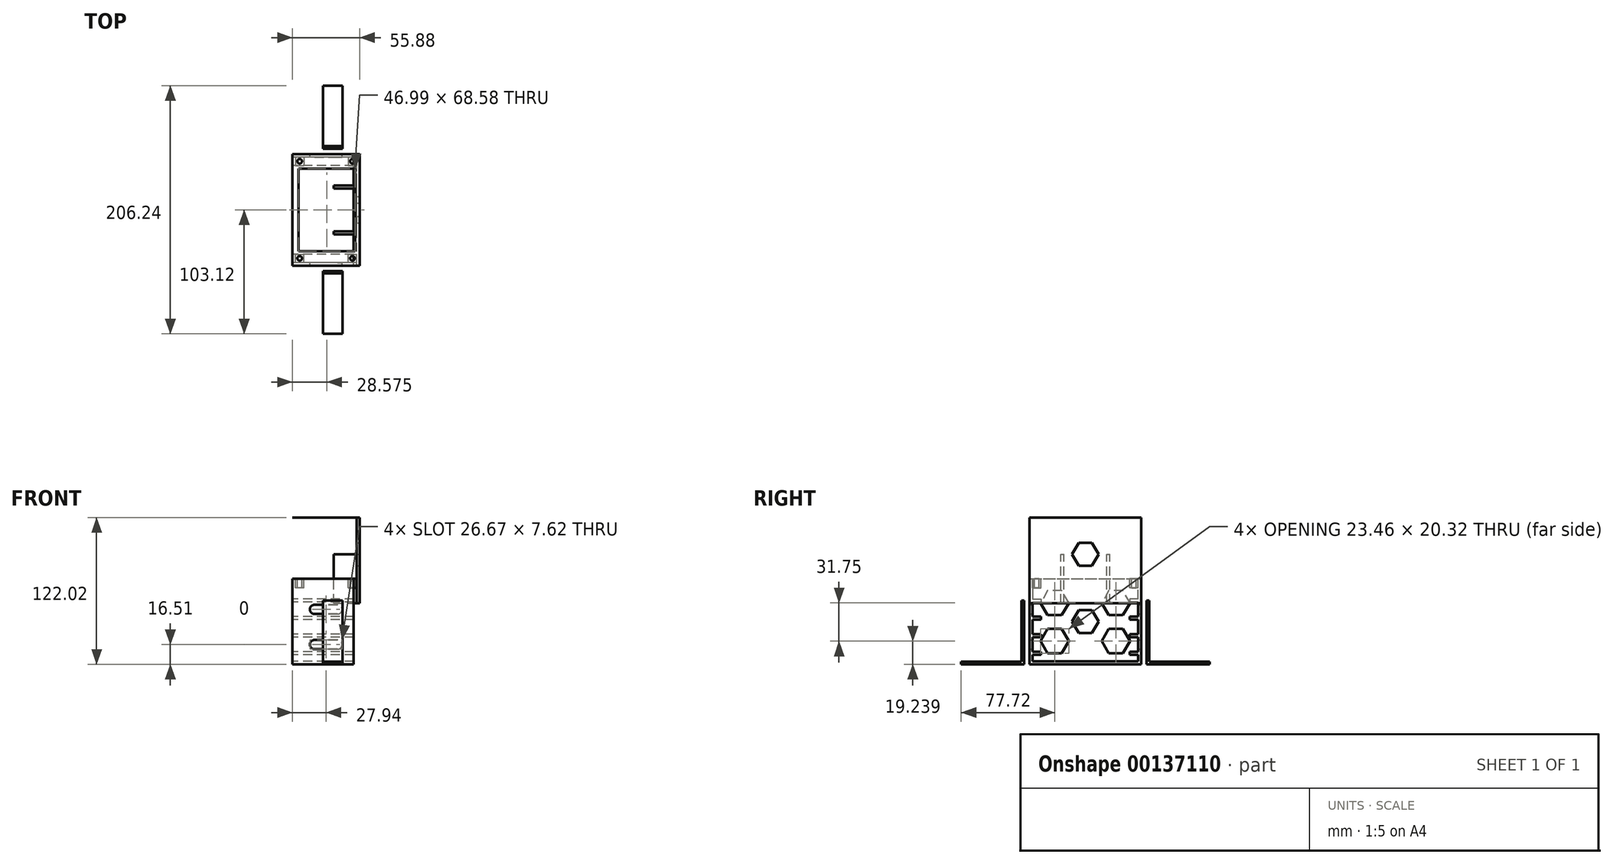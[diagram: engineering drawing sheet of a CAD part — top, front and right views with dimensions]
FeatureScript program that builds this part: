
annotation { "Feature Type Name" : "Feature", "Feature Type Description" : "" }
export const myFeature = defineFeature(function(context is Context, id is Id, definition is map)
    precondition{}
    {
        {
            assignVariable(context, id + "F0", {"name" : "sideWidth", "anyValue" : .1});
        }
        {
            var Q0;
            Q0=qCreatedBy(makeId("Right.planeOp"),FACE);
            var sketch = newSketch(context, id + "F1", { "sketchPlane" : qUnion([Q0])});
            skLineSegment(sketch, "E0.bottom", {"start": v(-50.8, 0) * mm, "end": v(-52.96, 0) * mm});
            skLineSegment(sketch, "E0.top", {"start": v(-50.8, 52.96) * mm, "end": v(-52.96, 52.96) * mm});
            skLineSegment(sketch, "E0.left", {"start": v(-50.8, 0) * mm, "end": v(-50.8, 52.96) * mm});
            skLineSegment(sketch, "E0.right", {"start": v(-52.96, 0) * mm, "end": v(-52.96, 52.96) * mm});
            skLineSegment(sketch, "E1.bottom", {"start": v(-50.8, 0) * mm, "end": v(-103.12, 0) * mm});
            skLineSegment(sketch, "E1.top", {"start": v(-50.8, 2.16) * mm, "end": v(-103.12, 2.16) * mm});
            skLineSegment(sketch, "E1.left", {"start": v(-50.8, 0) * mm, "end": v(-50.8, 2.16) * mm});
            skLineSegment(sketch, "E1.right", {"start": v(-103.12, 0) * mm, "end": v(-103.12, 2.16) * mm});
            skLineSegment(sketch, "E2.bottom", {"start": v(50.8, 0) * mm, "end": v(52.96, 0) * mm});
            skLineSegment(sketch, "E2.top", {"start": v(50.8, 52.96) * mm, "end": v(52.96, 52.96) * mm});
            skLineSegment(sketch, "E2.left", {"start": v(50.8, 0) * mm, "end": v(50.8, 52.96) * mm});
            skLineSegment(sketch, "E2.right", {"start": v(52.96, 0) * mm, "end": v(52.96, 52.96) * mm});
            skLineSegment(sketch, "E3.bottom", {"start": v(50.8, 0) * mm, "end": v(103.12, 0) * mm});
            skLineSegment(sketch, "E3.top", {"start": v(50.8, 2.16) * mm, "end": v(103.12, 2.16) * mm});
            skLineSegment(sketch, "E3.left", {"start": v(50.8, 0) * mm, "end": v(50.8, 2.16) * mm});
            skLineSegment(sketch, "E3.right", {"start": v(103.12, 0) * mm, "end": v(103.12, 2.16) * mm});
            skLineSegment(sketch, "E4", {"start": v(-50.8, 0) * mm, "end": v(0, 0) * mm, "construction": true});
            skLineSegment(sketch, "E5", {"start": v(0, 0) * mm, "end": v(50.8, 0) * mm, "construction": true});
            skSolve(sketch);
        }
        {
            var Q0;
            Q0 = qSketchRegion(id + "F1", true);
            extrude(context, id + "F2", {"entities" : qUnion([Q0]), "depth" : 16.13 * mm});
        }
        {
            var Q0;
            Q0=qCreatedBy(makeId("Right.planeOp"),FACE);
            cPlane(context, id + "F3", {"entities" : qUnion([Q0]), "cplaneType" : CPlaneType.OFFSET, "offset" : 25.4 * mm, "oppositeDirection" : true, "width" : 152.4 * mm, "height" : 152.4 * mm});
        }
        {
            var Q0;
            Q0=qCreatedBy(id+"F3.planeOp",FACE);
            var sketch = newSketch(context, id + "F4", { "sketchPlane" : qUnion([Q0])});
            skLineSegment(sketch, "E6.bottom", {"start": v(-46.35, 0) * mm, "end": v(46.35, 0) * mm});
            skLineSegment(sketch, "E6.top", {"start": v(-46.36, 71.12) * mm, "end": v(46.36, 71.12) * mm});
            skLineSegment(sketch, "E6.left", {"start": v(-46.35, 0) * mm, "end": v(-46.36, 71.12) * mm});
            skLineSegment(sketch, "E6.right", {"start": v(46.35, 0) * mm, "end": v(46.35, 71.12) * mm});
            skSolve(sketch);
        }
        {
            var Q0;
            Q0 = qSketchRegion(id + "F4", true);
            extrude(context, id + "F5", {"entities" : qUnion([Q0]), "depth" : (getVariable(context, 'sideWidth')) * mm});
        }
        {
            var Q0;
            Q0=makeQuery(id+"F5.opExtrude","CAP_FACE",FACE,{"disambiguationData":[OSD([sQuery(id+"F4.wireOp",EDGE,"E6.bottom"),sQuery(id+"F4.wireOp",EDGE,"E6.top"),sQuery(id+"F4.wireOp",EDGE,"E6.left"),sQuery(id+"F4.wireOp",EDGE,"E6.right")])],"isStart":false});
            var sketch = newSketch(context, id + "F6", { "sketchPlane" : qUnion([Q0])});
            skLineSegment(sketch, "E7.bottom", {"start": v(-46.36, 71.12) * mm, "end": v(-43.82, 71.12) * mm});
            skLineSegment(sketch, "E7.top", {"start": v(-46.36, 0) * mm, "end": v(-43.82, 0) * mm});
            skLineSegment(sketch, "E7.left", {"start": v(-46.36, 71.12) * mm, "end": v(-46.36, 0) * mm});
            skLineSegment(sketch, "E7.right", {"start": v(-43.82, 71.12) * mm, "end": v(-43.82, 0) * mm});
            skLineSegment(sketch, "E8.bottom", {"start": v(-46.36, 0) * mm, "end": v(46.36, 0) * mm});
            skLineSegment(sketch, "E8.top", {"start": v(-46.36, 2.54) * mm, "end": v(46.35, 2.54) * mm});
            skLineSegment(sketch, "E8.left", {"start": v(-46.36, 0) * mm, "end": v(-46.36, 2.54) * mm});
            skLineSegment(sketch, "E8.right", {"start": v(46.35, 0) * mm, "end": v(46.35, 2.54) * mm});
            skLineSegment(sketch, "E9.bottom", {"start": v(46.35, 0) * mm, "end": v(43.81, 0) * mm});
            skLineSegment(sketch, "E9.top", {"start": v(46.35, 71.12) * mm, "end": v(43.81, 71.12) * mm});
            skLineSegment(sketch, "E9.left", {"start": v(46.35, 0) * mm, "end": v(46.35, 71.12) * mm});
            skLineSegment(sketch, "E9.right", {"start": v(43.81, 0) * mm, "end": v(43.81, 71.12) * mm});
            skLineSegment(sketch, "E10.bottom", {"start": v(-46.36, 0) * mm, "end": v(-27.62, 0) * mm});
            skLineSegment(sketch, "E10.top", {"start": v(-46.36, 53.98) * mm, "end": v(-27.62, 53.98) * mm, "construction": true});
            skLineSegment(sketch, "E10.left", {"start": v(-46.36, 0) * mm, "end": v(-46.36, 53.98) * mm});
            skLineSegment(sketch, "E10.right", {"start": v(-27.62, 0) * mm, "end": v(-27.62, 53.98) * mm, "construction": true});
            skLineSegment(sketch, "E11.bottom", {"start": v(46.35, 0) * mm, "end": v(27.62, 0) * mm});
            skLineSegment(sketch, "E11.top", {"start": v(46.35, 53.98) * mm, "end": v(27.62, 53.98) * mm, "construction": true});
            skLineSegment(sketch, "E11.left", {"start": v(46.36, 0) * mm, "end": v(46.35, 53.98) * mm});
            skLineSegment(sketch, "E11.right", {"start": v(27.62, 0) * mm, "end": v(27.62, 53.98) * mm, "construction": true});
            skLineSegment(sketch, "E12", {"start": v(-27.62, 53.98) * mm, "end": v(27.62, 53.98) * mm, "construction": true});
            skLineSegment(sketch, "E13.bottom", {"start": v(-43.82, 54.42) * mm, "end": v(-36.83, 54.42) * mm});
            skLineSegment(sketch, "E13.top", {"start": v(-43.82, 51.88) * mm, "end": v(-36.83, 51.88) * mm});
            skLineSegment(sketch, "E13.left", {"start": v(-43.82, 54.42) * mm, "end": v(-43.82, 51.88) * mm});
            skLineSegment(sketch, "E13.right", {"start": v(-36.83, 54.42) * mm, "end": v(-36.83, 51.88) * mm});
            skLineSegment(sketch, "E14.bottom", {"start": v(-43.82, 39.56) * mm, "end": v(-36.83, 39.56) * mm});
            skLineSegment(sketch, "E14.top", {"start": v(-43.82, 37.02) * mm, "end": v(-36.83, 37.02) * mm});
            skLineSegment(sketch, "E14.left", {"start": v(-43.82, 39.56) * mm, "end": v(-43.82, 37.02) * mm});
            skLineSegment(sketch, "E14.right", {"start": v(-36.83, 39.56) * mm, "end": v(-36.83, 37.02) * mm});
            skLineSegment(sketch, "E15.bottom", {"start": v(-43.82, 25.2) * mm, "end": v(-36.83, 25.2) * mm});
            skLineSegment(sketch, "E15.top", {"start": v(-43.82, 22.67) * mm, "end": v(-36.83, 22.67) * mm});
            skLineSegment(sketch, "E15.left", {"start": v(-43.82, 25.2) * mm, "end": v(-43.82, 22.67) * mm});
            skLineSegment(sketch, "E15.right", {"start": v(-36.83, 25.2) * mm, "end": v(-36.83, 22.67) * mm});
            skLineSegment(sketch, "E16.bottom", {"start": v(-43.82, 10.35) * mm, "end": v(-36.83, 10.35) * mm});
            skLineSegment(sketch, "E16.top", {"start": v(-43.82, 7.81) * mm, "end": v(-36.83, 7.81) * mm});
            skLineSegment(sketch, "E16.left", {"start": v(-43.82, 10.35) * mm, "end": v(-43.82, 7.81) * mm});
            skLineSegment(sketch, "E16.right", {"start": v(-36.83, 10.35) * mm, "end": v(-36.83, 7.81) * mm});
            skLineSegment(sketch, "E17.bottom", {"start": v(43.81, 54.42) * mm, "end": v(36.83, 54.42) * mm});
            skLineSegment(sketch, "E17.top", {"start": v(43.81, 51.88) * mm, "end": v(36.83, 51.88) * mm});
            skLineSegment(sketch, "E17.left", {"start": v(43.81, 54.42) * mm, "end": v(43.81, 51.88) * mm});
            skLineSegment(sketch, "E17.right", {"start": v(36.83, 54.42) * mm, "end": v(36.83, 51.88) * mm});
            skLineSegment(sketch, "E18.bottom", {"start": v(43.81, 39.56) * mm, "end": v(36.83, 39.56) * mm});
            skLineSegment(sketch, "E18.top", {"start": v(43.81, 37.02) * mm, "end": v(36.83, 37.02) * mm});
            skLineSegment(sketch, "E18.left", {"start": v(43.81, 39.56) * mm, "end": v(43.81, 37.02) * mm});
            skLineSegment(sketch, "E18.right", {"start": v(36.83, 39.56) * mm, "end": v(36.83, 37.02) * mm});
            skLineSegment(sketch, "E19.bottom", {"start": v(43.81, 25.2) * mm, "end": v(36.83, 25.2) * mm});
            skLineSegment(sketch, "E19.top", {"start": v(43.81, 22.67) * mm, "end": v(36.83, 22.67) * mm});
            skLineSegment(sketch, "E19.left", {"start": v(43.81, 25.2) * mm, "end": v(43.81, 22.67) * mm});
            skLineSegment(sketch, "E19.right", {"start": v(36.83, 25.2) * mm, "end": v(36.83, 22.67) * mm});
            skLineSegment(sketch, "E20.bottom", {"start": v(43.81, 10.35) * mm, "end": v(36.83, 10.35) * mm});
            skLineSegment(sketch, "E20.top", {"start": v(43.81, 7.81) * mm, "end": v(36.83, 7.81) * mm});
            skLineSegment(sketch, "E20.left", {"start": v(43.81, 10.35) * mm, "end": v(43.81, 7.81) * mm});
            skLineSegment(sketch, "E20.right", {"start": v(36.83, 10.35) * mm, "end": v(36.83, 7.81) * mm});
            skLineSegment(sketch, "E21", {"start": v(-36.83, 51.88) * mm, "end": v(-36.83, 39.56) * mm, "construction": true});
            skLineSegment(sketch, "E22", {"start": v(-36.83, 22.67) * mm, "end": v(-36.83, 10.35) * mm, "construction": true});
            skLineSegment(sketch, "E23", {"start": v(36.83, 51.88) * mm, "end": v(36.83, 39.56) * mm, "construction": true});
            skLineSegment(sketch, "E24", {"start": v(36.83, 22.67) * mm, "end": v(36.83, 10.35) * mm, "construction": true});
            skPoint(sketch, "E25", {"position": v(-36.83, 45.72) * mm});
            skPoint(sketch, "E26", {"position": v(-36.83, 16.51) * mm});
            skSolve(sketch);
        }
        {
            var Q0;
            Q0 = qSketchRegion(id + "F6", true);
            extrude(context, id + "F7", {"entities" : qUnion([Q0]), "operationType" : NewBodyOperationType.ADD, "depth" : 50.8 * mm});
        }
        {
            var Q0;
            Q0=makeQuery(id+"F7.boolean.opBoolean","MERGE",FACE,{"derivedFrom":[makeQuery(id+"F5.opExtrude","SWEPT_FACE",FACE,{"disambiguationData":[OSD([sQuery(id+"F4.wireOp",EDGE,"E6.top")])]}),makeQuery(id+"F7.opExtrude","SWEPT_FACE",FACE,{"disambiguationData":[OSD([sQuery(id+"F6.wireOp",EDGE,"E7.bottom")])]}),makeQuery(id+"F7.opExtrude","SWEPT_FACE",FACE,{"disambiguationData":[OSD([sQuery(id+"F6.wireOp",EDGE,"E9.top")])]})]});
            var sketch = newSketch(context, id + "F8", { "sketchPlane" : qUnion([Q0])});
            skLineSegment(sketch, "E27.bottom", {"start": v(-22.86, 43.81) * mm, "end": v(-15.88, 43.81) * mm});
            skLineSegment(sketch, "E27.top", {"start": v(-22.86, 36.83) * mm, "end": v(-15.88, 36.83) * mm});
            skLineSegment(sketch, "E27.left", {"start": v(-22.86, 43.81) * mm, "end": v(-22.86, 36.83) * mm});
            skLineSegment(sketch, "E27.right", {"start": v(-15.88, 43.81) * mm, "end": v(-15.88, 36.83) * mm});
            skLineSegment(sketch, "E28.bottom", {"start": v(20.96, 43.81) * mm, "end": v(27.94, 43.81) * mm});
            skLineSegment(sketch, "E28.top", {"start": v(20.96, 36.83) * mm, "end": v(27.94, 36.83) * mm});
            skLineSegment(sketch, "E28.left", {"start": v(20.96, 43.81) * mm, "end": v(20.96, 36.83) * mm});
            skLineSegment(sketch, "E28.right", {"start": v(27.94, 43.81) * mm, "end": v(27.94, 36.83) * mm});
            skLineSegment(sketch, "E29.bottom", {"start": v(-22.86, -43.82) * mm, "end": v(-15.87, -43.82) * mm});
            skLineSegment(sketch, "E29.top", {"start": v(-22.86, -36.83) * mm, "end": v(-15.87, -36.83) * mm});
            skLineSegment(sketch, "E29.left", {"start": v(-22.86, -43.81) * mm, "end": v(-22.86, -36.83) * mm});
            skLineSegment(sketch, "E29.right", {"start": v(-15.87, -43.81) * mm, "end": v(-15.87, -36.83) * mm});
            skLineSegment(sketch, "E30.bottom", {"start": v(20.96, -43.82) * mm, "end": v(27.94, -43.82) * mm});
            skLineSegment(sketch, "E30.top", {"start": v(20.96, -36.83) * mm, "end": v(27.94, -36.83) * mm});
            skLineSegment(sketch, "E30.left", {"start": v(20.96, -43.81) * mm, "end": v(20.96, -36.83) * mm});
            skLineSegment(sketch, "E30.right", {"start": v(27.94, -43.81) * mm, "end": v(27.94, -36.83) * mm});
            skCircle(sketch, "E31", {"center": v(-19.37, 40.32) * mm, "radius": 1.9 * mm});
            skPoint(sketch, "E31.centerSnap0", {"position": v(-19.37, 36.83) * mm});
            skPoint(sketch, "E31.centerSnap1", {"position": v(-15.88, 40.32) * mm});
            skCircle(sketch, "E32", {"center": v(24.45, 40.32) * mm, "radius": 1.9 * mm});
            skPoint(sketch, "E32.centerSnap0", {"position": v(24.45, 36.83) * mm});
            skPoint(sketch, "E32.centerSnap1", {"position": v(27.94, 40.32) * mm});
            skCircle(sketch, "E33", {"center": v(24.45, -40.32) * mm, "radius": 1.9 * mm});
            skPoint(sketch, "E33.centerSnap0", {"position": v(24.45, -43.82) * mm});
            skPoint(sketch, "E33.centerSnap1", {"position": v(27.94, -40.32) * mm});
            skCircle(sketch, "E34", {"center": v(-19.37, -40.32) * mm, "radius": 1.9 * mm});
            skPoint(sketch, "E34.centerSnap0", {"position": v(-19.37, -43.82) * mm});
            skPoint(sketch, "E34.centerSnap1", {"position": v(-15.87, -40.32) * mm});
            skSolve(sketch);
        }
        {
            var Q0;
            Q0 = qSketchRegion(id + "F8", true);
            extrude(context, id + "F9", {"entities" : qUnion([Q0]), "operationType" : NewBodyOperationType.ADD, "oppositeDirection" : true, "depth" : 7.62 * mm});
        }
        {
            var Q0;
            {var subQ0=sQuery(id+"F6.wireOp",EDGE,"E7.right");Q0=makeQuery(id+"F7.opExtrude","SWEPT_FACE",FACE,{"disambiguationData":[OSD([subQ0]),TDD([makeQuery(id+"F6.imprint","IMPRINT",EDGE,{"disambiguationData":[TD([[makeQuery(id+"F6.imprint","INTERSECT",VERTEX,{"derivedFrom":[subQ0,sQuery(id+"F6.wireOp",EDGE,"E13.top"),sQuery(id+"F6.wireOp",EDGE,"E13.left")]}),-1.0]])],"derivedFrom":subQ0})])]});}
            var sketch = newSketch(context, id + "F10", { "sketchPlane" : qUnion([Q0])});
            skLineSegment(sketch, "E35.bottom", {"start": v(-12.07, 49.53) * mm, "end": v(6.98, 49.53) * mm});
            skLineSegment(sketch, "E35.top", {"start": v(-12.07, 41.91) * mm, "end": v(6.98, 41.91) * mm});
            skLineSegment(sketch, "E35.left", {"start": v(-12.07, 49.53) * mm, "end": v(-12.07, 41.91) * mm});
            skLineSegment(sketch, "E35.right", {"start": v(6.98, 49.53) * mm, "end": v(6.98, 41.91) * mm});
            skLineSegment(sketch, "E36.bottom", {"start": v(-12.07, 20.32) * mm, "end": v(6.98, 20.32) * mm});
            skLineSegment(sketch, "E36.top", {"start": v(-12.07, 12.7) * mm, "end": v(6.98, 12.7) * mm});
            skLineSegment(sketch, "E36.left", {"start": v(-12.07, 20.32) * mm, "end": v(-12.07, 12.7) * mm});
            skLineSegment(sketch, "E36.right", {"start": v(6.98, 20.32) * mm, "end": v(6.98, 12.7) * mm});
            skArc(sketch, "E37", {"start": v(-12.07, 49.53) * mm, "mid": v(-15.88, 45.72) * mm, "end": v(-12.07, 41.91) * mm});
            skArc(sketch, "E38", {"start": v(6.98, 41.91) * mm, "mid": v(10.8, 45.72) * mm, "end": v(6.98, 49.53) * mm});
            skArc(sketch, "E39", {"start": v(-12.07, 20.32) * mm, "mid": v(-15.88, 16.51) * mm, "end": v(-12.07, 12.7) * mm});
            skArc(sketch, "E40", {"start": v(6.98, 12.7) * mm, "mid": v(10.8, 16.51) * mm, "end": v(6.98, 20.32) * mm});
            skPoint(sketch, "E41", {"position": v(-2.54, 41.91) * mm});
            skPoint(sketch, "E42", {"position": v(-2.54, 20.32) * mm});
            skLineSegment(sketch, "E43", {"start": v(-27.94, 39.56) * mm, "end": v(-27.94, 51.88) * mm, "construction": true});
            skLineSegment(sketch, "E44", {"start": v(-27.94, 22.67) * mm, "end": v(-27.94, 10.35) * mm, "construction": true});
            skPoint(sketch, "E45", {"position": v(-27.94, 16.51) * mm});
            skPoint(sketch, "E46", {"position": v(-27.94, 45.72) * mm});
            skSolve(sketch);
        }
        {
            var Q0;
            Q0 = qSketchRegion(id + "F10", true);
            extrude(context, id + "F11", {"entities" : qUnion([Q0]), "operationType" : NewBodyOperationType.REMOVE, "endBound" : BoundingType.UP_TO_NEXT, "oppositeDirection" : true, "depth" : 25.4 * mm, "hasSecondDirection" : true, "secondDirectionBound" : SecondDirectionBoundingType.THROUGH_ALL, "secondDirectionOppositeDirection" : false, "secondDirectionDepth" : 25.4 * mm});
        }
        {
            var Q0;
            Q0=makeQuery(id+"F7.opExtrude","SWEPT_FACE",FACE,{"disambiguationData":[OSD([sQuery(id+"F6.wireOp",EDGE,"E8.top")])]});
            var sketch = newSketch(context, id + "F12", { "sketchPlane" : qUnion([Q0])});
            skLineSegment(sketch, "E47", {"start": v(5.72, -43.82) * mm, "end": v(5.71, 43.81) * mm, "construction": true});
            skCircle(sketch, "E48", {"center": v(5.71, 20.32) * mm, "radius": 1.59 * mm});
            skCircle(sketch, "E49", {"center": v(5.72, -20.32) * mm, "radius": 1.59 * mm});
            skPoint(sketch, "E50", {"position": v(5.72, 0) * mm});
            skSolve(sketch);
        }
        {
            var Q0;
            Q0=makeQuery(id+"F9.boolean.opBoolean","MERGE",FACE,{"derivedFrom":[makeQuery(id+"F7.boolean.opBoolean","MERGE",FACE,{"derivedFrom":[makeQuery(id+"F5.opExtrude","SWEPT_FACE",FACE,{"disambiguationData":[OSD([sQuery(id+"F4.wireOp",EDGE,"E6.top")])]}),makeQuery(id+"F7.opExtrude","SWEPT_FACE",FACE,{"disambiguationData":[OSD([sQuery(id+"F6.wireOp",EDGE,"E7.bottom")])]}),makeQuery(id+"F7.opExtrude","SWEPT_FACE",FACE,{"disambiguationData":[OSD([sQuery(id+"F6.wireOp",EDGE,"E9.top")])]})]}),makeQuery(id+"F9.opExtrude","CAP_FACE",FACE,{"disambiguationData":[OSD([sQuery(id+"F8.wireOp",EDGE,"E27.bottom"),sQuery(id+"F8.wireOp",EDGE,"E27.top"),sQuery(id+"F8.wireOp",EDGE,"E27.left"),sQuery(id+"F8.wireOp",EDGE,"E27.right"),sQuery(id+"F8.wireOp",EDGE,"E31")])],"isStart":true}),makeQuery(id+"F9.opExtrude","CAP_FACE",FACE,{"disambiguationData":[OSD([sQuery(id+"F8.wireOp",EDGE,"E28.bottom"),sQuery(id+"F8.wireOp",EDGE,"E28.top"),sQuery(id+"F8.wireOp",EDGE,"E28.left"),sQuery(id+"F8.wireOp",EDGE,"E28.right"),sQuery(id+"F8.wireOp",EDGE,"E32")])],"isStart":true}),makeQuery(id+"F9.opExtrude","CAP_FACE",FACE,{"disambiguationData":[OSD([sQuery(id+"F8.wireOp",EDGE,"E29.bottom"),sQuery(id+"F8.wireOp",EDGE,"E29.top"),sQuery(id+"F8.wireOp",EDGE,"E29.left"),sQuery(id+"F8.wireOp",EDGE,"E29.right"),sQuery(id+"F8.wireOp",EDGE,"E34")])],"isStart":true}),makeQuery(id+"F9.opExtrude","CAP_FACE",FACE,{"disambiguationData":[OSD([sQuery(id+"F8.wireOp",EDGE,"E30.bottom"),sQuery(id+"F8.wireOp",EDGE,"E30.top"),sQuery(id+"F8.wireOp",EDGE,"E30.left"),sQuery(id+"F8.wireOp",EDGE,"E30.right"),sQuery(id+"F8.wireOp",EDGE,"E33")])],"isStart":true})]});
            cPlane(context, id + "F13", {"entities" : qUnion([Q0]), "cplaneType" : CPlaneType.OFFSET, "offset" : 50.8 * mm, "width" : 152.4 * mm, "height" : 152.4 * mm});
        }
        {
            var Q0;
            Q0=qCreatedBy(id+"F13.planeOp",FACE);
            var sketch = newSketch(context, id + "F14", { "sketchPlane" : qUnion([Q0])});
            skLineSegment(sketch, "E51.bottom", {"start": v(27.94, -46.36) * mm, "end": v(-25.4, -46.36) * mm});
            skLineSegment(sketch, "E51.top", {"start": v(27.94, 46.35) * mm, "end": v(-25.4, 46.35) * mm});
            skLineSegment(sketch, "E51.left", {"start": v(27.94, -46.36) * mm, "end": v(27.94, 46.35) * mm});
            skLineSegment(sketch, "E51.right", {"start": v(-25.4, -46.36) * mm, "end": v(-25.4, 46.35) * mm});
            skLineSegment(sketch, "E52.bottom", {"start": v(-20.32, 34.29) * mm, "end": v(26.67, 34.3) * mm});
            skLineSegment(sketch, "E52.top", {"start": v(-20.32, -34.3) * mm, "end": v(26.67, -34.3) * mm});
            skLineSegment(sketch, "E52.left", {"start": v(-20.32, 34.29) * mm, "end": v(-20.32, -34.3) * mm});
            skLineSegment(sketch, "E52.right", {"start": v(26.67, 34.3) * mm, "end": v(26.67, -34.3) * mm});
            skLineSegment(sketch, "E53", {"start": v(3.17, 36.83) * mm, "end": v(3.17, 34.29) * mm, "construction": true});
            skLineSegment(sketch, "E54", {"start": v(-20.32, 0) * mm, "end": v(-22.86, 0) * mm, "construction": true});
            skLineSegment(sketch, "E55", {"start": v(26.67, 0) * mm, "end": v(29.2, 0) * mm, "construction": true});
            skLineSegment(sketch, "E56", {"start": v(3.18, -34.3) * mm, "end": v(3.18, -36.83) * mm, "construction": true});
            skLineSegment(sketch, "E57.bottom", {"start": v(27.94, -46.36) * mm, "end": v(30.48, -46.36) * mm});
            skLineSegment(sketch, "E57.top", {"start": v(27.94, 46.35) * mm, "end": v(30.48, 46.35) * mm});
            skLineSegment(sketch, "E57.right", {"start": v(30.48, -46.36) * mm, "end": v(30.48, 46.35) * mm});
            skCircle(sketch, "E58", {"center": v(-19.37, 40.32) * mm, "radius": 1.9 * mm});
            skCircle(sketch, "E59", {"center": v(24.45, 40.32) * mm, "radius": 1.9 * mm});
            skCircle(sketch, "E60", {"center": v(-19.37, -40.32) * mm, "radius": 1.9 * mm});
            skCircle(sketch, "E61", {"center": v(24.45, -40.32) * mm, "radius": 1.9 * mm});
            skSolve(sketch);
        }
        {
            var Q0;
            Q0 = qSketchRegion(id + "F14", true);
            extrude(context, id + "F15", {"entities" : qUnion([Q0]), "depth" : (getVariable(context, 'sideWidth')) * mm});
        }
        {
            var Q0;
            Q0=makeQuery(id+"F15.opExtrude","CAP_FACE",FACE,{"disambiguationData":[OSD([sQuery(id+"F14.wireOp",EDGE,"E51.bottom"),sQuery(id+"F14.wireOp",EDGE,"E51.top"),sQuery(id+"F14.wireOp",EDGE,"E51.right"),sQuery(id+"F14.wireOp",EDGE,"E52.bottom"),sQuery(id+"F14.wireOp",EDGE,"E52.top"),sQuery(id+"F14.wireOp",EDGE,"E52.left"),sQuery(id+"F14.wireOp",EDGE,"E52.right"),sQuery(id+"F14.wireOp",EDGE,"E57.bottom"),sQuery(id+"F14.wireOp",EDGE,"E57.top"),sQuery(id+"F14.wireOp",EDGE,"E57.right")])],"isStart":true});
            var sketch = newSketch(context, id + "F16", { "sketchPlane" : qUnion([Q0])});
            skLineSegment(sketch, "E62.bottom", {"start": v(30.48, 46.36) * mm, "end": v(27.94, 46.36) * mm});
            skLineSegment(sketch, "E62.top", {"start": v(30.48, -46.35) * mm, "end": v(27.94, -46.35) * mm});
            skLineSegment(sketch, "E62.left", {"start": v(30.48, 46.36) * mm, "end": v(30.48, -46.35) * mm});
            skLineSegment(sketch, "E62.right", {"start": v(27.94, 46.36) * mm, "end": v(27.94, -46.35) * mm});
            skSolve(sketch);
        }
        {
            var Q0;
            Q0 = qSketchRegion(id + "F16", true);
            extrude(context, id + "F17", {"entities" : qUnion([Q0]), "operationType" : NewBodyOperationType.ADD, "depth" : 71.12 * mm});
        }
        {
            var Q0;
            Q0=makeQuery(id+"F17.boolean.opBoolean","MERGE",FACE,{"derivedFrom":[makeQuery(id+"F15.opExtrude","SWEPT_FACE",FACE,{"disambiguationData":[OSD([sQuery(id+"F14.wireOp",EDGE,"E57.right")])]}),makeQuery(id+"F17.opExtrude","SWEPT_FACE",FACE,{"disambiguationData":[OSD([sQuery(id+"F16.wireOp",EDGE,"E62.left")])]})]});
            var sketch = newSketch(context, id + "F18", { "sketchPlane" : qUnion([Q0])});
            skCircle(sketch, "E63.cCircle", {"center": v(0, 91.44) * mm, "radius": 9.53 * mm, "construction": true});
            skPoint(sketch, "E63.cCircle.centerSnap0", {"position": v(0, 50.8) * mm});
            skLineSegment(sketch, "E63.0", {"start": v(-5.5, 100.97) * mm, "end": v(5.5, 100.97) * mm});
            skLineSegment(sketch, "E63.1", {"start": v(5.5, 100.97) * mm, "end": v(11, 91.44) * mm});
            skLineSegment(sketch, "E63.2", {"start": v(11, 91.44) * mm, "end": v(5.5, 81.92) * mm});
            skLineSegment(sketch, "E63.3", {"start": v(5.5, 81.92) * mm, "end": v(-5.5, 81.92) * mm});
            skLineSegment(sketch, "E63.4", {"start": v(-5.5, 81.92) * mm, "end": v(-11, 91.44) * mm});
            skLineSegment(sketch, "E63.5", {"start": v(-11, 91.44) * mm, "end": v(-5.5, 100.97) * mm});
            skPoint(sketch, "E63.0.midPoint", {"position": v(0, 100.97) * mm});
            skSolve(sketch);
        }
        {
            var Q0;
            Q0 = qSketchRegion(id + "F18", true);
            extrude(context, id + "F19", {"entities" : qUnion([Q0]), "operationType" : NewBodyOperationType.REMOVE, "endBound" : BoundingType.UP_TO_NEXT, "oppositeDirection" : true, "depth" : 25.4 * mm});
        }
        {
            var Q0;
            Q0=makeQuery(id+"F17.opExtrude","SWEPT_FACE",FACE,{"disambiguationData":[OSD([sQuery(id+"F16.wireOp",EDGE,"E62.right")])]});
            var sketch = newSketch(context, id + "F20", { "sketchPlane" : qUnion([Q0])});
            skLineSegment(sketch, "E64.bottom", {"start": v(20.32, 50.8) * mm, "end": v(17.78, 50.8) * mm});
            skLineSegment(sketch, "E64.top", {"start": v(20.32, 91.44) * mm, "end": v(17.78, 91.44) * mm});
            skLineSegment(sketch, "E64.left", {"start": v(20.32, 50.8) * mm, "end": v(20.32, 91.44) * mm});
            skLineSegment(sketch, "E64.right", {"start": v(17.78, 50.8) * mm, "end": v(17.78, 91.44) * mm});
            skLineSegment(sketch, "E65.bottom", {"start": v(-17.78, 50.8) * mm, "end": v(-20.32, 50.8) * mm});
            skLineSegment(sketch, "E65.top", {"start": v(-17.78, 91.44) * mm, "end": v(-20.32, 91.44) * mm});
            skLineSegment(sketch, "E65.left", {"start": v(-17.78, 50.8) * mm, "end": v(-17.78, 91.44) * mm});
            skLineSegment(sketch, "E65.right", {"start": v(-20.32, 50.8) * mm, "end": v(-20.32, 91.44) * mm});
            skLineSegment(sketch, "E66", {"start": v(17.78, 71.12) * mm, "end": v(-17.78, 71.12) * mm, "construction": true});
            skPoint(sketch, "E67", {"position": v(0, 71.12) * mm});
            skSolve(sketch);
        }
        {
            var Q0;
            Q0 = qSketchRegion(id + "F20", true);
            extrude(context, id + "F21", {"entities" : qUnion([Q0]), "operationType" : NewBodyOperationType.ADD, "depth" : 19.05 * mm});
        }
        {
            var Q0;
            Q0=makeQuery(id+"F5.opExtrude","CAP_FACE",FACE,{"disambiguationData":[OSD([sQuery(id+"F4.wireOp",EDGE,"E6.bottom"),sQuery(id+"F4.wireOp",EDGE,"E6.top"),sQuery(id+"F4.wireOp",EDGE,"E6.left"),sQuery(id+"F4.wireOp",EDGE,"E6.right")])],"isStart":true});
            var sketch = newSketch(context, id + "F22", { "sketchPlane" : qUnion([Q0])});
            skCircle(sketch, "E68.cCircle", {"center": v(0, 35.56) * mm, "radius": 9.53 * mm, "construction": true});
            skLineSegment(sketch, "E68.0", {"start": v(-5.5, 45.09) * mm, "end": v(5.5, 45.09) * mm});
            skLineSegment(sketch, "E68.1", {"start": v(5.5, 45.09) * mm, "end": v(11, 35.56) * mm});
            skLineSegment(sketch, "E68.2", {"start": v(11, 35.56) * mm, "end": v(5.5, 26.04) * mm});
            skLineSegment(sketch, "E68.3", {"start": v(5.5, 26.04) * mm, "end": v(-5.5, 26.04) * mm});
            skLineSegment(sketch, "E68.4", {"start": v(-5.5, 26.04) * mm, "end": v(-11, 35.56) * mm});
            skLineSegment(sketch, "E68.5", {"start": v(-11, 35.56) * mm, "end": v(-5.5, 45.08) * mm});
            skPoint(sketch, "E68.0.midPoint", {"position": v(0, 45.08) * mm});
            skCircle(sketch, "E69.cCircle", {"center": v(-25.4, 50.99) * mm, "radius": 10.16 * mm, "construction": true});
            skLineSegment(sketch, "E69.0", {"start": v(-31.27, 61.15) * mm, "end": v(-19.53, 61.15) * mm});
            skLineSegment(sketch, "E69.1", {"start": v(-19.53, 61.15) * mm, "end": v(-13.67, 50.99) * mm});
            skLineSegment(sketch, "E69.2", {"start": v(-13.67, 50.99) * mm, "end": v(-19.53, 40.83) * mm});
            skLineSegment(sketch, "E69.3", {"start": v(-19.53, 40.83) * mm, "end": v(-31.27, 40.83) * mm});
            skLineSegment(sketch, "E69.4", {"start": v(-31.27, 40.83) * mm, "end": v(-37.13, 50.99) * mm});
            skLineSegment(sketch, "E69.5", {"start": v(-37.13, 50.99) * mm, "end": v(-31.27, 61.15) * mm});
            skPoint(sketch, "E69.0.midPoint", {"position": v(-25.4, 61.15) * mm});
            skCircle(sketch, "E70.cCircle", {"center": v(-25.4, 19.24) * mm, "radius": 10.16 * mm, "construction": true});
            skLineSegment(sketch, "E70.0", {"start": v(-31.27, 29.4) * mm, "end": v(-19.53, 29.4) * mm});
            skLineSegment(sketch, "E70.1", {"start": v(-19.53, 29.4) * mm, "end": v(-13.67, 19.24) * mm});
            skLineSegment(sketch, "E70.2", {"start": v(-13.67, 19.24) * mm, "end": v(-19.53, 9.08) * mm});
            skLineSegment(sketch, "E70.3", {"start": v(-19.53, 9.08) * mm, "end": v(-31.27, 9.08) * mm});
            skLineSegment(sketch, "E70.4", {"start": v(-31.27, 9.08) * mm, "end": v(-37.13, 19.24) * mm});
            skLineSegment(sketch, "E70.5", {"start": v(-37.13, 19.24) * mm, "end": v(-31.27, 29.4) * mm});
            skPoint(sketch, "E70.0.midPoint", {"position": v(-25.4, 29.4) * mm});
            skCircle(sketch, "E71.cCircle", {"center": v(25.4, 50.99) * mm, "radius": 10.16 * mm, "construction": true});
            skLineSegment(sketch, "E71.0", {"start": v(19.53, 61.15) * mm, "end": v(31.27, 61.15) * mm});
            skLineSegment(sketch, "E71.1", {"start": v(31.27, 61.15) * mm, "end": v(37.13, 50.99) * mm});
            skLineSegment(sketch, "E71.2", {"start": v(37.13, 50.99) * mm, "end": v(31.27, 40.83) * mm});
            skLineSegment(sketch, "E71.3", {"start": v(31.27, 40.83) * mm, "end": v(19.53, 40.83) * mm});
            skLineSegment(sketch, "E71.4", {"start": v(19.53, 40.83) * mm, "end": v(13.67, 50.99) * mm});
            skLineSegment(sketch, "E71.5", {"start": v(13.67, 50.99) * mm, "end": v(19.53, 61.15) * mm});
            skPoint(sketch, "E71.0.midPoint", {"position": v(25.4, 61.15) * mm});
            skCircle(sketch, "E72.cCircle", {"center": v(25.4, 19.24) * mm, "radius": 10.16 * mm, "construction": true});
            skPoint(sketch, "E72.cCircle.centerSnap0", {"position": v(25.4, 40.83) * mm});
            skLineSegment(sketch, "E72.0", {"start": v(31.27, 9.08) * mm, "end": v(19.53, 9.08) * mm});
            skLineSegment(sketch, "E72.1", {"start": v(19.53, 9.08) * mm, "end": v(13.67, 19.24) * mm});
            skLineSegment(sketch, "E72.2", {"start": v(13.67, 19.24) * mm, "end": v(19.53, 29.4) * mm});
            skLineSegment(sketch, "E72.3", {"start": v(19.53, 29.4) * mm, "end": v(31.27, 29.4) * mm});
            skLineSegment(sketch, "E72.4", {"start": v(31.27, 29.4) * mm, "end": v(37.13, 19.24) * mm});
            skLineSegment(sketch, "E72.5", {"start": v(37.13, 19.24) * mm, "end": v(31.27, 9.08) * mm});
            skPoint(sketch, "E72.0.midPoint", {"position": v(25.4, 9.08) * mm});
            skPoint(sketch, "E73", {"position": v(-46.35, 35.56) * mm});
            skPoint(sketch, "E74", {"position": v(0, 71.12) * mm});
            skPoint(sketch, "E75.endSnap0", {"position": v(-8.25, 40.32) * mm});
            skLineSegment(sketch, "E76", {"start": v(16.6, 45.9) * mm, "end": v(8.25, 40.32) * mm, "construction": true});
            skLineSegment(sketch, "E77", {"start": v(16.6, 24.32) * mm, "end": v(8.25, 30.8) * mm, "construction": true});
            skLineSegment(sketch, "E78", {"start": v(-8.25, 30.8) * mm, "end": v(-16.6, 24.32) * mm, "construction": true});
            skLineSegment(sketch, "E79", {"start": v(-16.6, 45.9) * mm, "end": v(-8.25, 40.32) * mm, "construction": true});
            skSolve(sketch);
        }
        {
            var Q0;
            Q0 = qSketchRegion(id + "F22", true);
            extrude(context, id + "F23", {"entities" : qUnion([Q0]), "operationType" : NewBodyOperationType.REMOVE, "endBound" : BoundingType.UP_TO_NEXT, "oppositeDirection" : true, "depth" : 25.4 * mm});
        }
    });
